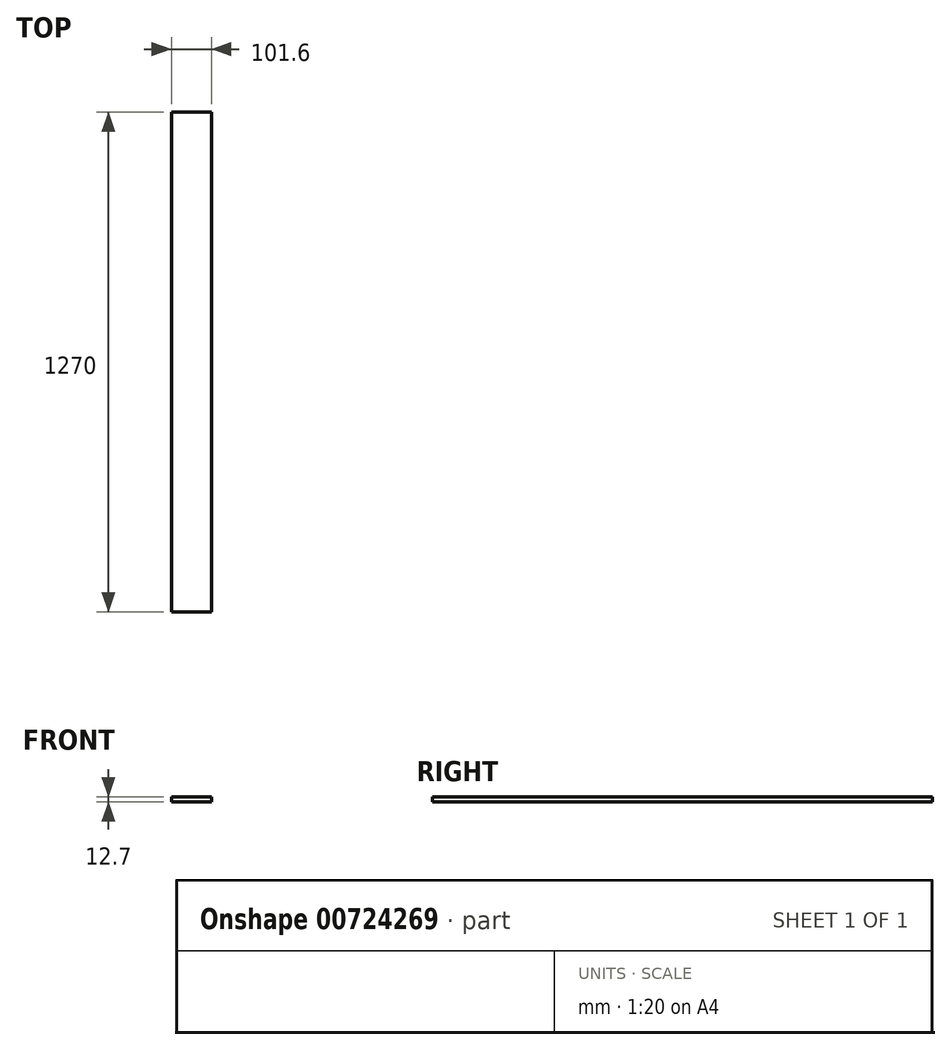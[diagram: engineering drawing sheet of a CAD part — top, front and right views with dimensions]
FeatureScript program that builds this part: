
annotation { "Feature Type Name" : "Feature", "Feature Type Description" : "" }
export const myFeature = defineFeature(function(context is Context, id is Id, definition is map)
    precondition{}
    {
        {
            var Q0;
            Q0=qCreatedBy(makeId("Top.planeOp"),FACE);
            var sketch = newSketch(context, id + "F0", { "sketchPlane" : qUnion([Q0])});
            skLineSegment(sketch, "E0.bottom", {"start": v(50.8, 635) * mm, "end": v(-50.8, 635) * mm});
            skLineSegment(sketch, "E0.top", {"start": v(50.8, -635) * mm, "end": v(-50.8, -635) * mm});
            skLineSegment(sketch, "E0.left", {"start": v(50.8, 635) * mm, "end": v(50.8, -635) * mm});
            skLineSegment(sketch, "E0.right", {"start": v(-50.8, 635) * mm, "end": v(-50.8, -635) * mm});
            skPoint(sketch, "E0.middle", {"position": v(0, 0) * mm});
            skSolve(sketch);
        }
        {
            var Q0;
            Q0 = qSketchRegion(id + "F0", true);
            extrude(context, id + "F1", {"entities" : qUnion([Q0]), "depth" : 12.7 * mm, "offsetDistance" : 25.4 * mm});
        }
        {
            var Q0;
            Q0=makeQuery(id+"F1.opExtrude","SWEPT_BODY",BODY,{"disambiguationData":[OSD([sQuery(id+"F0.wireOp",EDGE,"E0.bottom"),sQuery(id+"F0.wireOp",EDGE,"E0.top"),sQuery(id+"F0.wireOp",EDGE,"E0.left"),sQuery(id+"F0.wireOp",EDGE,"E0.right")])]});
            transform(context, id + "F2", {"entities" : qUnion([Q0]), "transformType" : TransformType.TRANSLATION_3D, "dx" : 0 * mm, "dy" : 0 * mm, "dz" : 0 * mm, "makeCopy" : true});
        }
    });
